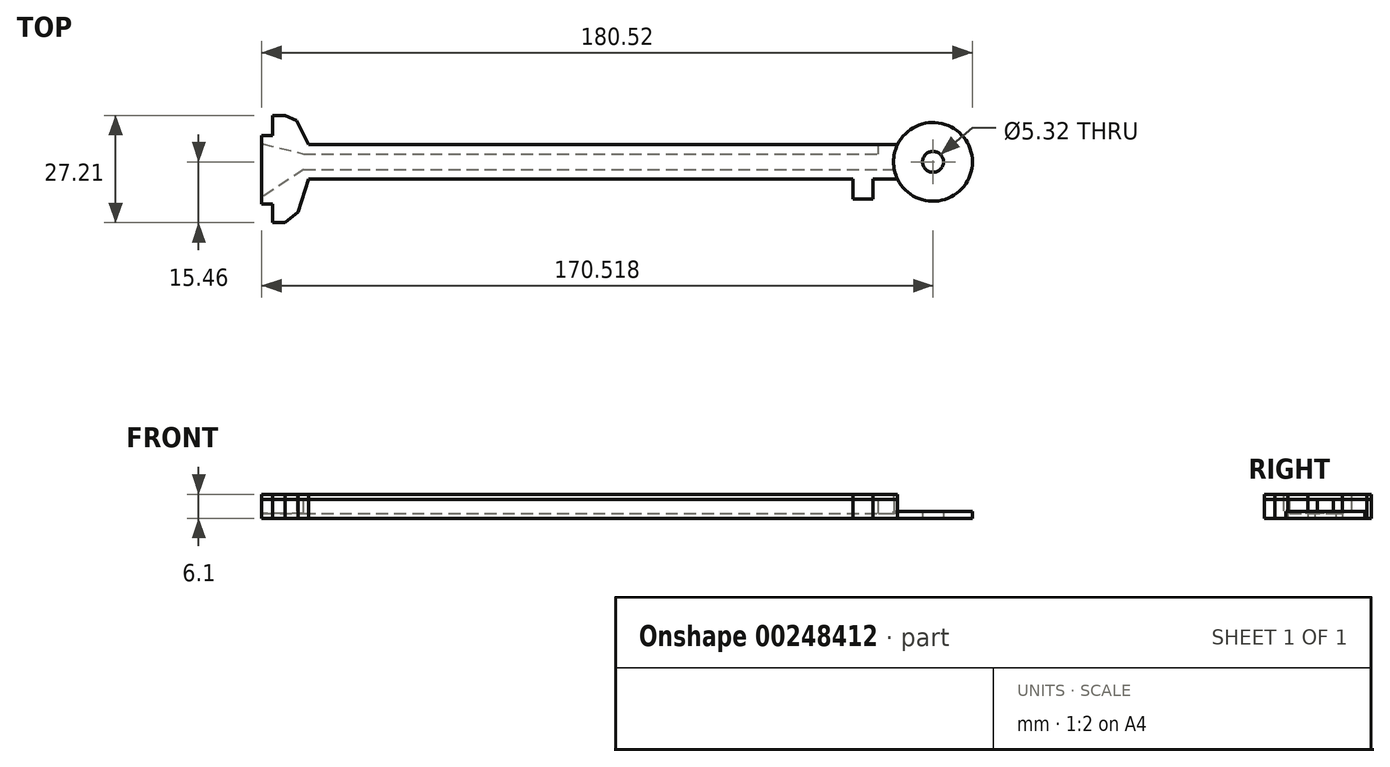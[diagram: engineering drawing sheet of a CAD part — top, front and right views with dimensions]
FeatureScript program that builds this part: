
annotation { "Feature Type Name" : "Feature", "Feature Type Description" : "" }
export const myFeature = defineFeature(function(context is Context, id is Id, definition is map)
    precondition{}
    {
        {
            var Q0;
            Q0=qCreatedBy(makeId("Top.planeOp"),FACE);
            var sketch = newSketch(context, id + "F0", { "sketchPlane" : qUnion([Q0])});
            skArc(sketch, "E0", {"start": v(71.25, -4.36) * mm, "mid": v(90.26, 0) * mm, "end": v(71.25, 4.36) * mm});
            skLineSegment(sketch, "E1.MirrorCS", {"start": v(71.25, -4.36) * mm, "end": v(64.98, -4.36) * mm});
            skLineSegment(sketch, "E2", {"start": v(-87.47, 11.75) * mm, "end": v(-84.31, 11.75) * mm});
            skLineSegment(sketch, "E3", {"start": v(-84.31, -15.46) * mm, "end": v(-87.47, -15.46) * mm});
            skLineSegment(sketch, "E4", {"start": v(-84.31, -15.46) * mm, "end": v(-81, -12.78) * mm});
            skLineSegment(sketch, "E5", {"start": v(-90.26, -10.7) * mm, "end": v(-87.47, -10.7) * mm});
            skLineSegment(sketch, "E6", {"start": v(-90.26, 6.63) * mm, "end": v(-87.47, 6.63) * mm});
            skLineSegment(sketch, "E7.trimOffspring", {"start": v(-87.47, -10.7) * mm, "end": v(-87.47, -15.46) * mm});
            skCircle(sketch, "E8", {"center": v(80.26, 0) * mm, "radius": 2.66 * mm});
            skLineSegment(sketch, "E9", {"start": v(-78.35, -4.36) * mm, "end": v(-81, -12.78) * mm});
            skLineSegment(sketch, "E10", {"start": v(-90.26, 6.63) * mm, "end": v(-90.26, -10.7) * mm});
            skLineSegment(sketch, "E11", {"start": v(-87.47, 6.63) * mm, "end": v(-87.47, 11.75) * mm});
            skLineSegment(sketch, "E12", {"start": v(-84.31, 11.75) * mm, "end": v(-81.37, 10.5) * mm});
            skLineSegment(sketch, "E13", {"start": v(-81.37, 10.5) * mm, "end": v(-78.35, 4.36) * mm});
            skLineSegment(sketch, "E14.MirrorCS", {"start": v(59.89, -9.45) * mm, "end": v(64.98, -9.45) * mm});
            skLineSegment(sketch, "E15.MirrorCS", {"start": v(59.89, -4.36) * mm, "end": v(59.89, -9.45) * mm});
            skLineSegment(sketch, "E16.MirrorCS", {"start": v(64.98, -9.45) * mm, "end": v(64.98, -4.36) * mm});
            skLineSegment(sketch, "E17", {"start": v(-78.35, 4.36) * mm, "end": v(71.25, 4.36) * mm});
            skLineSegment(sketch, "E18.trimOffspring", {"start": v(59.89, -4.36) * mm, "end": v(-78.35, -4.36) * mm});
            skSolve(sketch);
        }
        {
            var Q0;
            Q0 = qSketchRegion(id + "F0", true);
            extrude(context, id + "F1", {"entities" : qUnion([Q0]), "depth" : 4.83 * mm, "offsetDistance" : 25.4 * mm});
        }
        {
            var Q0;
            Q0=makeQuery(id+"F1.opExtrude","CAP_FACE",FACE,{"disambiguationData":[OSD([sQuery(id+"F0.wireOp",EDGE,"E0"),sQuery(id+"F0.wireOp",EDGE,"E1.MirrorCS"),sQuery(id+"F0.wireOp",EDGE,"XnEWtmCP-9tPJ-yOSt-lhv1-N9fbx313V1B5"),sQuery(id+"F0.wireOp",EDGE,"E2"),sQuery(id+"F0.wireOp",EDGE,"E3"),sQuery(id+"F0.wireOp",EDGE,"MlFvFiwd-k4Bk-zik2-qDNQ-lbmeR9Z7n4gK"),sQuery(id+"F0.wireOp",EDGE,"E4"),sQuery(id+"F0.wireOp",EDGE,"E5"),sQuery(id+"F0.wireOp",EDGE,"E6"),sQuery(id+"F0.wireOp",EDGE,"E7.trimOffspring"),sQuery(id+"F0.wireOp",EDGE,"E8"),sQuery(id+"F0.wireOp",EDGE,"Wqcn3GFb-zzja-a08h-2OyD-edHPtJF5RdgS"),sQuery(id+"F0.wireOp",EDGE,"E9"),sQuery(id+"F0.wireOp",EDGE,"E10"),sQuery(id+"F0.wireOp",EDGE,"EsfQBZd6-kOI4-ZdZB-V1TJ-pURWITAcBYtD"),sQuery(id+"F0.wireOp",EDGE,"IyjwJboQ-TShV-24cN-XNoa-WljtGkf8nw3d"),sQuery(id+"F0.wireOp",EDGE,"Jg2juNGl-A5cI-pBwn-6ZwR-xGGsyObEcXjS"),sQuery(id+"F0.wireOp",EDGE,"LetQRDky-Ub2q-PBws-39Ry-aP8J6iVG1mi9"),sQuery(id+"F0.wireOp",EDGE,"96EzJLEu-xqdx-xk4f-GQrl-AYoTv4likgWj")])],"isStart":false});
            var sketch = newSketch(context, id + "F2", { "sketchPlane" : qUnion([Q0])});
            skCircle(sketch, "E19", {"center": v(80.26, 0) * mm, "radius": 10.03 * mm});
            skLineSegment(sketch, "E20", {"start": v(71.27, 4.48) * mm, "end": v(71.27, 4.45) * mm});
            skLineSegment(sketch, "E21", {"start": v(-79.6, 2.03) * mm, "end": v(66.46, 2.03) * mm});
            skLineSegment(sketch, "E22", {"start": v(-90.26, 4.65) * mm, "end": v(-79.6, 2.03) * mm});
            skLineSegment(sketch, "E23.MirrorCS", {"start": v(66.46, 2) * mm, "end": v(66.46, 4.48) * mm});
            skLineSegment(sketch, "E24.MirrorCS", {"start": v(66.46, 4.48) * mm, "end": v(71.28, 4.48) * mm});
            skLineSegment(sketch, "E25", {"start": v(-79.6, -2) * mm, "end": v(70.43, -2) * mm});
            skLineSegment(sketch, "E26", {"start": v(-79.6, -2) * mm, "end": v(-90.26, -9.01) * mm});
            skLineSegment(sketch, "E27", {"start": v(-90.26, -9.01) * mm, "end": v(-90.26, 4.65) * mm});
            skSolve(sketch);
        }
        {
            var Q0;
            {var subQ1=sQuery(id+"F2.wireOp",EDGE,"E21");Q0=makeQuery(id+"F2.imprint","IMPRINT",FACE,{"disambiguationData":[TD([[makeQuery(id+"F2.imprint","IMPRINT",EDGE,{"derivedFrom":subQ1}),-1.0]])]});}
            extrude(context, id + "F3", {"entities" : qUnion([Q0]), "operationType" : NewBodyOperationType.REMOVE, "oppositeDirection" : true, "depth" : 3.56 * mm, "offsetDistance" : 25.4 * mm});
        }
        {
            var Q0;
            {var subQ1=makeQuery(id+"F1.opExtrude","CAP_EDGE",EDGE,{"disambiguationData":[OSD([sQuery(id+"F0.wireOp",EDGE,"E0")])],"isStart":false});Q0=makeQuery(id+"F2.imprint","IMPRINT",FACE,{"disambiguationData":[TD([[makeQuery(id+"F2.imprint","IMPRINT",EDGE,{"derivedFrom":subQ1}),1.0]])]});}
            extrude(context, id + "F4", {"entities" : qUnion([Q0]), "operationType" : NewBodyOperationType.REMOVE, "oppositeDirection" : true, "depth" : 3.05 * mm, "offsetDistance" : 25.4 * mm});
        }
        {
            var Q0;
            {var subQ0=sQuery(id+"F0.wireOp",EDGE,"E10");var subQ1=sQuery(id+"F0.wireOp",EDGE,"E11");var subQ2=sQuery(id+"F0.wireOp",EDGE,"E6");var subQ3=sQuery(id+"F0.wireOp",EDGE,"E17");var subQ4=sQuery(id+"F0.wireOp",EDGE,"E2");var subQ5=sQuery(id+"F0.wireOp",EDGE,"E13");var subQ6=sQuery(id+"F0.wireOp",EDGE,"E12");Q0=makeQuery(id+"F3.boolean.opBoolean","SPLIT",FACE,{"disambiguationData":[TD([makeQuery(id+"F1.opExtrude","SWEPT_FACE",FACE,{"disambiguationData":[OSD([subQ4])]})])],"derivedFrom":makeQuery(id+"F1.opExtrude","CAP_FACE",FACE,{"disambiguationData":[OSD([sQuery(id+"F0.wireOp",EDGE,"E0"),sQuery(id+"F0.wireOp",EDGE,"E1.MirrorCS"),subQ4,sQuery(id+"F0.wireOp",EDGE,"E3"),sQuery(id+"F0.wireOp",EDGE,"E4"),sQuery(id+"F0.wireOp",EDGE,"E5"),subQ2,sQuery(id+"F0.wireOp",EDGE,"E7.trimOffspring"),sQuery(id+"F0.wireOp",EDGE,"E8"),sQuery(id+"F0.wireOp",EDGE,"E9"),subQ0,subQ1,subQ6,subQ5,sQuery(id+"F0.wireOp",EDGE,"E14.MirrorCS"),sQuery(id+"F0.wireOp",EDGE,"E15.MirrorCS"),sQuery(id+"F0.wireOp",EDGE,"E16.MirrorCS"),subQ3,sQuery(id+"F0.wireOp",EDGE,"E18.trimOffspring")])],"isStart":false})});}
            var sketch = newSketch(context, id + "F5", { "sketchPlane" : qUnion([Q0])});
            skLineSegment(sketch, "E28.MirrorCS", {"start": v(71.25, -4.36) * mm, "end": v(64.98, -4.36) * mm});
            skLineSegment(sketch, "E29", {"start": v(-87.47, 11.75) * mm, "end": v(-84.31, 11.75) * mm});
            skLineSegment(sketch, "E30", {"start": v(-84.31, -15.46) * mm, "end": v(-87.47, -15.46) * mm});
            skLineSegment(sketch, "E31", {"start": v(-84.31, -15.46) * mm, "end": v(-81, -12.78) * mm});
            skLineSegment(sketch, "E32", {"start": v(-90.26, -10.7) * mm, "end": v(-87.47, -10.7) * mm});
            skLineSegment(sketch, "E33", {"start": v(-90.26, 6.63) * mm, "end": v(-87.47, 6.63) * mm});
            skLineSegment(sketch, "E34.trimOffspring", {"start": v(-87.47, -10.7) * mm, "end": v(-87.47, -15.46) * mm});
            skCircle(sketch, "E35", {"center": v(80.26, 0) * mm, "radius": 2.66 * mm});
            skLineSegment(sketch, "E36", {"start": v(-78.35, -4.36) * mm, "end": v(-81, -12.78) * mm});
            skLineSegment(sketch, "E37", {"start": v(-90.26, 6.63) * mm, "end": v(-90.26, -10.7) * mm});
            skLineSegment(sketch, "E38", {"start": v(-87.47, 6.63) * mm, "end": v(-87.47, 11.75) * mm});
            skLineSegment(sketch, "E39", {"start": v(-84.31, 11.75) * mm, "end": v(-81.37, 10.5) * mm});
            skLineSegment(sketch, "E40", {"start": v(-81.37, 10.5) * mm, "end": v(-78.35, 4.36) * mm});
            skArc(sketch, "E41", {"start": v(71.25, 4.36) * mm, "mid": v(70.24, 0) * mm, "end": v(71.25, -4.36) * mm});
            skLineSegment(sketch, "E42.MirrorCS", {"start": v(59.89, -9.45) * mm, "end": v(64.98, -9.45) * mm});
            skLineSegment(sketch, "E43.MirrorCS", {"start": v(59.89, -4.36) * mm, "end": v(59.89, -9.45) * mm});
            skLineSegment(sketch, "E44.MirrorCS", {"start": v(64.98, -9.45) * mm, "end": v(64.98, -4.36) * mm});
            skLineSegment(sketch, "E45.trimOffspring", {"start": v(59.89, -4.36) * mm, "end": v(-78.35, -4.36) * mm});
            skLineSegment(sketch, "E46", {"start": v(-78.35, 4.36) * mm, "end": v(71.25, 4.36) * mm});
            skSolve(sketch);
        }
        {
            var Q0;
            Q0 = qSketchRegion(id + "F5", true);
            extrude(context, id + "F6", {"entities" : qUnion([Q0]), "depth" : 1.27 * mm, "offsetDistance" : 25.4 * mm});
        }
        {
            var Q0;
            Q0=makeQuery(id+"F6.opExtrude","SWEPT_BODY",BODY,{"disambiguationData":[OSD([sQuery(id+"F5.wireOp",EDGE,"E35")])]});
            deleteBodies(context, id + "F7", {"entities" : qUnion([Q0])});
        }
    });
